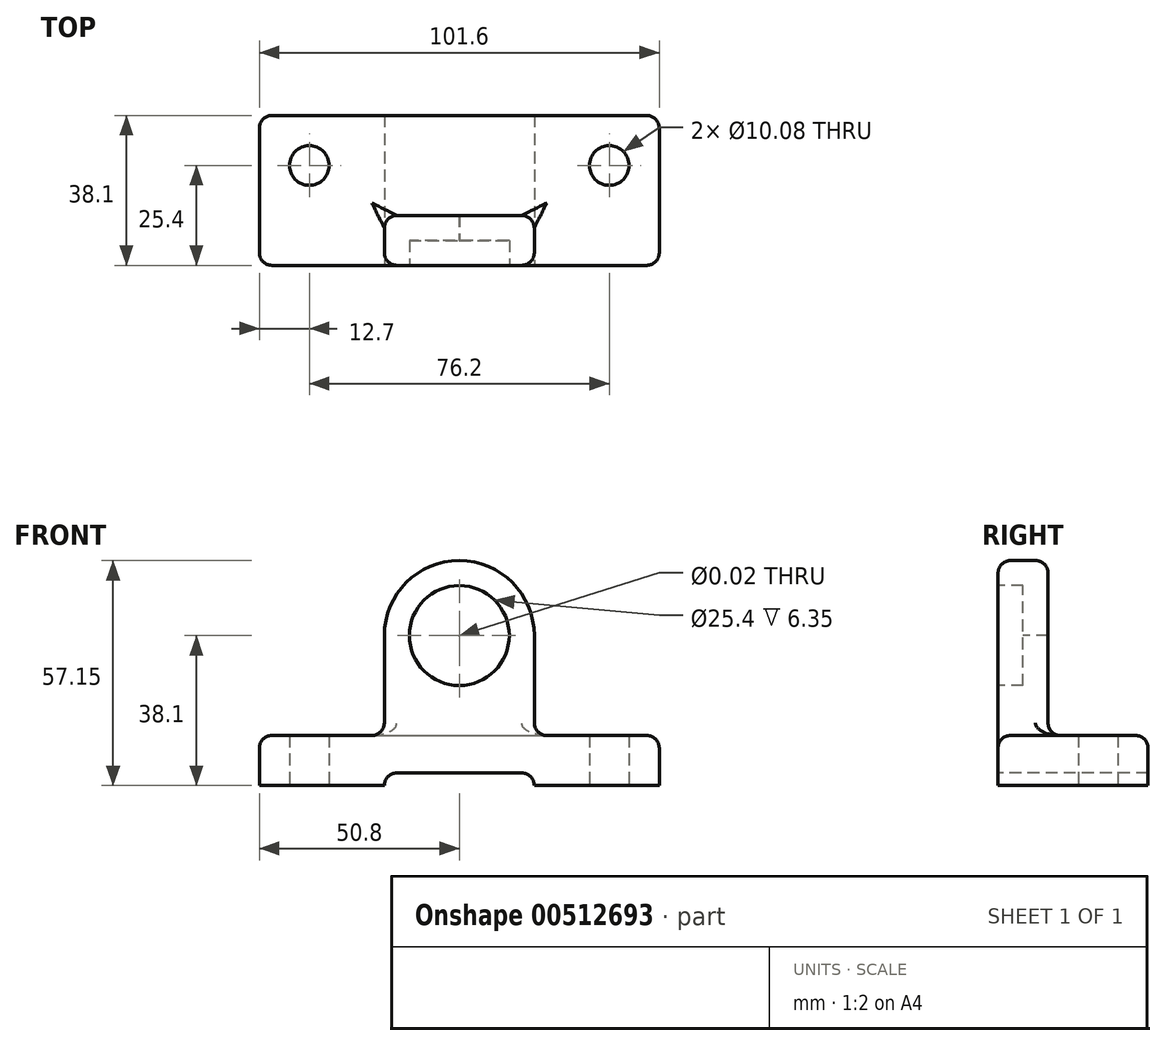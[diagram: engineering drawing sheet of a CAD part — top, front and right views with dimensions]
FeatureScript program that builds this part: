
annotation { "Feature Type Name" : "Feature", "Feature Type Description" : "" }
export const myFeature = defineFeature(function(context is Context, id is Id, definition is map)
    precondition{}
    {
        {
            var Q0;
            Q0=qCreatedBy(makeId("Top.planeOp"),FACE);
            var sketch = newSketch(context, id + "F0", { "sketchPlane" : qUnion([Q0])});
            skLineSegment(sketch, "E0.bottom", {"start": v(0, 0) * mm, "end": v(101.6, 0) * mm});
            skLineSegment(sketch, "E0.top", {"start": v(0, 38.1) * mm, "end": v(101.6, 38.1) * mm});
            skLineSegment(sketch, "E0.left", {"start": v(0, 0) * mm, "end": v(0, 38.1) * mm});
            skLineSegment(sketch, "E0.right", {"start": v(101.6, 0) * mm, "end": v(101.6, 38.1) * mm});
            skSolve(sketch);
        }
        {
            var Q0;
            Q0 = qSketchRegion(id + "F0", true);
            extrude(context, id + "F1", {"entities" : qUnion([Q0]), "depth" : 12.7 * mm});
        }
        {
            var Q0;
            Q0=qCreatedBy(makeId("Front.planeOp"),FACE);
            var sketch = newSketch(context, id + "F2", { "sketchPlane" : qUnion([Q0])});
            skLineSegment(sketch, "E1", {"start": v(31.75, 0) * mm, "end": v(31.75, 38.1) * mm});
            skArc(sketch, "E2", {"start": v(69.85, 38.1) * mm, "mid": v(50.8, 57.15) * mm, "end": v(31.75, 38.1) * mm});
            skLineSegment(sketch, "E3", {"start": v(69.85, 38.1) * mm, "end": v(69.85, 0) * mm});
            skLineSegment(sketch, "E4", {"start": v(31.75, 0) * mm, "end": v(69.85, 0) * mm});
            skSolve(sketch);
        }
        {
            var Q0;
            Q0 = qSketchRegion(id + "F2", true);
            extrude(context, id + "F3", {"entities" : qUnion([Q0]), "operationType" : NewBodyOperationType.ADD, "oppositeDirection" : true, "depth" : 12.7 * mm});
        }
        {
            var Q0;
            Q0=sQuery(id+"F2.wireOp",VERTEX,"E2.center");
            var Q1;
            Q1=makeQuery(id+"F1.opExtrude","SWEPT_BODY",BODY,{"disambiguationData":[OSD([sQuery(id+"F0.wireOp",EDGE,"E0.bottom"),sQuery(id+"F0.wireOp",EDGE,"E0.top"),sQuery(id+"F0.wireOp",EDGE,"E0.left"),sQuery(id+"F0.wireOp",EDGE,"E0.right")])]});
            hole(context, id + "F4", {"style" : HoleStyle.C_BORE, "endStyle" : HoleEndStyle.THROUGH, "standardTappedOrClearance" : lookupTablePath({ "standard" : "ANSI", "size" : "15/32 (0.47)", "type" : "Drilled" }), "standardBlindInLast" : lookupTablePath({ "standard" : "ANSI", "size" : "15/32", "type" : "Drilled" }), "holeDiameter" : 15 / 812.8 * mm, "cBoreDiameter" : 25.4 * mm, "cBoreDepth" : 6.35 * mm, "isTappedThrough" : true, "tappedDepth" : 12.7 * mm, "tapClearance" : 3, "locations" : qUnion([Q0]), "scope" : qUnion([Q1])});
        }
        {
            var Q0;
            Q0=qCreatedBy(makeId("Front.planeOp"),FACE);
            var sketch = newSketch(context, id + "F5", { "sketchPlane" : qUnion([Q0])});
            skLineSegment(sketch, "E5", {"start": v(69.85, 0) * mm, "end": v(69.85, 3.18) * mm});
            skLineSegment(sketch, "E6", {"start": v(69.85, 3.18) * mm, "end": v(31.75, 3.18) * mm});
            skLineSegment(sketch, "E7", {"start": v(31.75, 3.18) * mm, "end": v(31.75, 0) * mm});
            skLineSegment(sketch, "E8", {"start": v(31.75, 0) * mm, "end": v(69.85, 0) * mm});
            skSolve(sketch);
        }
        {
            var Q0;
            Q0 = qSketchRegion(id + "F5", true);
            extrude(context, id + "F6", {"entities" : qUnion([Q0]), "operationType" : NewBodyOperationType.REMOVE, "endBound" : BoundingType.THROUGH_ALL, "oppositeDirection" : true, "depth" : 25.4 * mm});
        }
        {
            var Q0;
            Q0=qCreatedBy(makeId("Top.planeOp"),FACE);
            var sketch = newSketch(context, id + "F7", { "sketchPlane" : qUnion([Q0])});
            skPoint(sketch, "E9", {"position": v(0, 25.4) * mm});
            skPoint(sketch, "E10", {"position": v(12.7, 25.4) * mm});
            skPoint(sketch, "E11", {"position": v(88.9, 38.1) * mm});
            skPoint(sketch, "E12", {"position": v(88.9, 25.4) * mm});
            skSolve(sketch);
        }
        {
            var Q0;
            Q0=sQuery(id+"F7.wireOp",VERTEX,"E12");
            var Q1;
            Q1=makeQuery(id+"F1.opExtrude","SWEPT_BODY",BODY,{"disambiguationData":[OSD([sQuery(id+"F0.wireOp",EDGE,"E0.bottom"),sQuery(id+"F0.wireOp",EDGE,"E0.top"),sQuery(id+"F0.wireOp",EDGE,"E0.left"),sQuery(id+"F0.wireOp",EDGE,"E0.right")])]});
            hole(context, id + "F8", {"style" : HoleStyle.SIMPLE, "endStyle" : HoleEndStyle.THROUGH, "oppositeDirection" : true, "standardTappedOrClearance" : lookupTablePath({ "standard" : "ANSI", "fit" : "Normal (ASME)", "size" : "3/8", "type" : "Clearance" }), "standardBlindInLast" : lookupTablePath({ "fit" : "Free", "standard" : "ANSI", "size" : "3/8", "type" : "Clearance" }), "holeDiameter" : 10.08 * mm, "isTappedThrough" : true, "tappedDepth" : 12.7 * mm, "tapClearance" : 3, "locations" : qUnion([Q0]), "scope" : qUnion([Q1])});
        }
        {
            var Q0;
            Q0=sQuery(id+"F7.wireOp",VERTEX,"E10");
            var Q1;
            Q1=makeQuery(id+"F1.opExtrude","SWEPT_BODY",BODY,{"disambiguationData":[OSD([sQuery(id+"F0.wireOp",EDGE,"E0.bottom"),sQuery(id+"F0.wireOp",EDGE,"E0.top"),sQuery(id+"F0.wireOp",EDGE,"E0.left"),sQuery(id+"F0.wireOp",EDGE,"E0.right")])]});
            hole(context, id + "F9", {"style" : HoleStyle.SIMPLE, "endStyle" : HoleEndStyle.THROUGH, "oppositeDirection" : true, "standardTappedOrClearance" : lookupTablePath({ "standard" : "ANSI", "fit" : "Normal (ASME)", "size" : "3/8", "type" : "Clearance" }), "standardBlindInLast" : lookupTablePath({ "fit" : "Free", "standard" : "ANSI", "size" : "3/8", "type" : "Clearance" }), "holeDiameter" : 10.08 * mm, "isTappedThrough" : true, "tappedDepth" : 12.7 * mm, "tapClearance" : 3, "locations" : qUnion([Q0]), "scope" : qUnion([Q1])});
        }
        {
            var Q0;
            Q0=makeQuery(id+"F1.opExtrude","SWEPT_EDGE",EDGE,{"disambiguationData":[OSD([sQuery(id+"F0.wireOp",EDGE,"E0.top"),sQuery(id+"F0.wireOp",EDGE,"E0.right")])]});
            fillet(context, id + "F10", {"entities" : qUnion([Q0]), "radius" : 3.17 * mm, "tangentPropagation" : true, "allowEdgeOverflow" : false});
        }
        {
            var Q0;
            Q0=makeQuery(id+"F1.opExtrude","SWEPT_EDGE",EDGE,{"disambiguationData":[OSD([sQuery(id+"F0.wireOp",EDGE,"E0.top"),sQuery(id+"F0.wireOp",EDGE,"E0.left")])]});
            fillet(context, id + "F11", {"entities" : qUnion([Q0]), "radius" : 3.17 * mm, "tangentPropagation" : true, "allowEdgeOverflow" : false});
        }
        {
            var Q0;
            Q0=makeQuery(id+"F1.opExtrude","SWEPT_EDGE",EDGE,{"disambiguationData":[OSD([sQuery(id+"F0.wireOp",EDGE,"E0.bottom"),sQuery(id+"F0.wireOp",EDGE,"E0.left")])]});
            fillet(context, id + "F12", {"entities" : qUnion([Q0]), "radius" : 3.17 * mm, "tangentPropagation" : true, "allowEdgeOverflow" : false});
        }
        {
            var Q0;
            Q0=makeQuery(id+"F1.opExtrude","SWEPT_EDGE",EDGE,{"disambiguationData":[OSD([sQuery(id+"F0.wireOp",EDGE,"E0.bottom"),sQuery(id+"F0.wireOp",EDGE,"E0.right")])]});
            fillet(context, id + "F13", {"entities" : qUnion([Q0]), "radius" : 3.17 * mm, "tangentPropagation" : true, "allowEdgeOverflow" : false});
        }
        {
            var Q0;
            Q0=makeQuery(id+"F6.boolean.opBoolean","COPY",EDGE,{"derivedFrom":makeQuery(id+"F6.opExtrude","SWEPT_EDGE",EDGE,{"disambiguationData":[OSD([sQuery(id+"F5.wireOp",EDGE,"E6"),sQuery(id+"F5.wireOp",EDGE,"E7")])]})});
            fillet(context, id + "F14", {"entities" : qUnion([Q0]), "radius" : 3.17 * mm, "tangentPropagation" : true, "allowEdgeOverflow" : false});
        }
        {
            var Q0;
            Q0=makeQuery(id+"F6.boolean.opBoolean","COPY",EDGE,{"derivedFrom":makeQuery(id+"F6.opExtrude","SWEPT_EDGE",EDGE,{"disambiguationData":[OSD([sQuery(id+"F5.wireOp",EDGE,"E5"),sQuery(id+"F5.wireOp",EDGE,"E6")])]})});
            fillet(context, id + "F15", {"entities" : qUnion([Q0]), "radius" : 3.17 * mm, "tangentPropagation" : true, "allowEdgeOverflow" : false});
        }
        {
            var Q0;
            Q0=makeQuery(id+"F1.opExtrude","CAP_EDGE",EDGE,{"disambiguationData":[OSD([sQuery(id+"F0.wireOp",EDGE,"E0.top")])],"isStart":false});
            fillet(context, id + "F16", {"entities" : qUnion([Q0]), "radius" : 3.17 * mm, "tangentPropagation" : true, "allowEdgeOverflow" : false});
        }
        {
            var Q0;
            Q0=makeQuery(id+"F3.boolean.opBoolean","INTERSECT",EDGE,{"derivedFrom":[makeQuery(id+"F1.opExtrude","CAP_FACE",FACE,{"disambiguationData":[OSD([sQuery(id+"F0.wireOp",EDGE,"E0.bottom"),sQuery(id+"F0.wireOp",EDGE,"E0.top"),sQuery(id+"F0.wireOp",EDGE,"E0.left"),sQuery(id+"F0.wireOp",EDGE,"E0.right")])],"isStart":false}),makeQuery(id+"F3.opExtrude","CAP_FACE",FACE,{"disambiguationData":[OSD([sQuery(id+"F2.wireOp",EDGE,"E1"),sQuery(id+"F2.wireOp",EDGE,"E2"),sQuery(id+"F2.wireOp",EDGE,"E3"),sQuery(id+"F2.wireOp",EDGE,"E4")])],"isStart":false})]});
            fillet(context, id + "F17", {"entities" : qUnion([Q0]), "radius" : 3.17 * mm, "tangentPropagation" : true, "allowEdgeOverflow" : false});
        }
        {
            var Q0;
            Q0=makeQuery(id+"F3.boolean.opBoolean","INTERSECT",EDGE,{"derivedFrom":[makeQuery(id+"F1.opExtrude","CAP_FACE",FACE,{"disambiguationData":[OSD([sQuery(id+"F0.wireOp",EDGE,"E0.bottom"),sQuery(id+"F0.wireOp",EDGE,"E0.top"),sQuery(id+"F0.wireOp",EDGE,"E0.left"),sQuery(id+"F0.wireOp",EDGE,"E0.right")])],"isStart":false}),makeQuery(id+"F3.opExtrude","SWEPT_FACE",FACE,{"disambiguationData":[OSD([sQuery(id+"F2.wireOp",EDGE,"E3")])]})]});
            fillet(context, id + "F18", {"entities" : qUnion([Q0]), "radius" : 3.17 * mm, "tangentPropagation" : true, "allowEdgeOverflow" : false});
        }
        {
            var Q0;
            Q0=makeQuery(id+"F3.boolean.opBoolean","INTERSECT",EDGE,{"derivedFrom":[makeQuery(id+"F1.opExtrude","CAP_FACE",FACE,{"disambiguationData":[OSD([sQuery(id+"F0.wireOp",EDGE,"E0.bottom"),sQuery(id+"F0.wireOp",EDGE,"E0.top"),sQuery(id+"F0.wireOp",EDGE,"E0.left"),sQuery(id+"F0.wireOp",EDGE,"E0.right")])],"isStart":false}),makeQuery(id+"F3.opExtrude","SWEPT_FACE",FACE,{"disambiguationData":[OSD([sQuery(id+"F2.wireOp",EDGE,"E1")])]})]});
            fillet(context, id + "F19", {"entities" : qUnion([Q0]), "radius" : 3.17 * mm, "tangentPropagation" : true, "allowEdgeOverflow" : false});
        }
        {
            var Q0;
            {var subQ0=makeQuery(id+"F3.opExtrude","CAP_FACE",FACE,{"disambiguationData":[OSD([sQuery(id+"F2.wireOp",EDGE,"E1"),sQuery(id+"F2.wireOp",EDGE,"E2"),sQuery(id+"F2.wireOp",EDGE,"E3"),sQuery(id+"F2.wireOp",EDGE,"E4")])],"isStart":false});Q0=makeQuery(id+"F17.opFillet","BLEND_EDGE",EDGE,{"blendedFrom":[makeQuery(id+"F3.boolean.opBoolean","INTERSECT",EDGE,{"derivedFrom":[makeQuery(id+"F1.opExtrude","CAP_FACE",FACE,{"disambiguationData":[OSD([sQuery(id+"F0.wireOp",EDGE,"E0.bottom"),sQuery(id+"F0.wireOp",EDGE,"E0.top"),sQuery(id+"F0.wireOp",EDGE,"E0.left"),sQuery(id+"F0.wireOp",EDGE,"E0.right")])],"isStart":false}),subQ0]}),subQ0],"blendedInto":[subQ0]});}
            var Q1;
            Q1=makeQuery(id+"F3.opExtrude","CAP_EDGE",EDGE,{"disambiguationData":[OSD([sQuery(id+"F2.wireOp",EDGE,"E1")])],"isStart":false});
            var Q2;
            Q2=makeQuery(id+"F3.opExtrude","CAP_EDGE",EDGE,{"disambiguationData":[OSD([sQuery(id+"F2.wireOp",EDGE,"E2")])],"isStart":false});
            var Q3;
            Q3=makeQuery(id+"F3.opExtrude","CAP_EDGE",EDGE,{"disambiguationData":[OSD([sQuery(id+"F2.wireOp",EDGE,"E3")])],"isStart":false});
            fillet(context, id + "F20", {"entities" : qUnion([Q0, Q1, Q2, Q3]), "radius" : 3.17 * mm, "tangentPropagation" : true, "allowEdgeOverflow" : false});
        }
        {
            var Q0;
            Q0=makeQuery(id+"F3.opExtrude","CAP_EDGE",EDGE,{"disambiguationData":[OSD([sQuery(id+"F2.wireOp",EDGE,"E1")])],"isStart":true});
            var Q1;
            Q1=makeQuery(id+"F3.opExtrude","CAP_EDGE",EDGE,{"disambiguationData":[OSD([sQuery(id+"F2.wireOp",EDGE,"E2")])],"isStart":true});
            fillet(context, id + "F21", {"entities" : qUnion([Q0, Q1]), "radius" : 3.17 * mm, "tangentPropagation" : true, "allowEdgeOverflow" : false});
        }
    });
